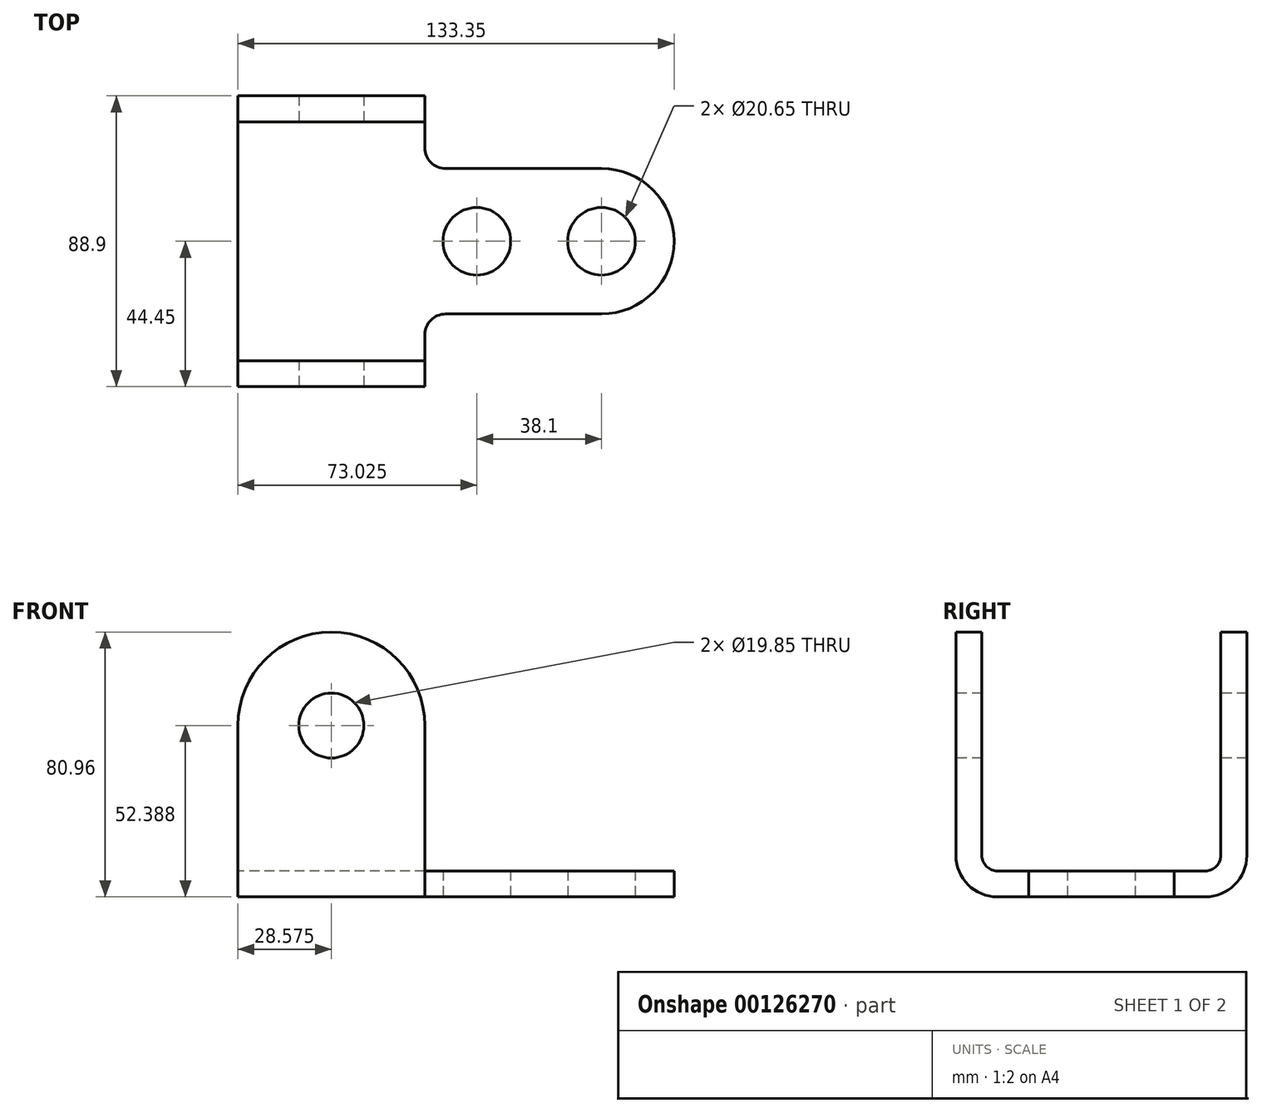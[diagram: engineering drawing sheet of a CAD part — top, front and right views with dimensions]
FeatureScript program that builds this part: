
annotation { "Feature Type Name" : "Feature", "Feature Type Description" : "" }
export const myFeature = defineFeature(function(context is Context, id is Id, definition is map)
    precondition{}
    {
        {
            var Q0;
            Q0=qCreatedBy(makeId("Top.planeOp"),FACE);
            var sketch = newSketch(context, id + "F0", { "sketchPlane" : qUnion([Q0])});
            skLineSegment(sketch, "E0", {"start": v(0, -44.45) * mm, "end": v(0, 44.45) * mm});
            skLineSegment(sketch, "E1", {"start": v(0, 44.45) * mm, "end": v(57.15, 44.45) * mm});
            skLineSegment(sketch, "E2", {"start": v(57.15, 44.45) * mm, "end": v(57.15, 28.57) * mm});
            skLineSegment(sketch, "E3", {"start": v(57.15, -44.45) * mm, "end": v(0, -44.45) * mm});
            skArc(sketch, "E4", {"start": v(111.12, 22.23) * mm, "mid": v(133.35, 0) * mm, "end": v(111.12, -22.23) * mm});
            skLineSegment(sketch, "E5", {"start": v(63.5, 22.22) * mm, "end": v(111.12, 22.23) * mm});
            skLineSegment(sketch, "E6", {"start": v(57.15, -44.45) * mm, "end": v(57.15, -28.58) * mm});
            skLineSegment(sketch, "E7", {"start": v(63.5, -22.23) * mm, "end": v(111.12, -22.23) * mm});
            skPoint(sketch, "E8.visualSharp", {"position": v(57.15, -22.23) * mm});
            skArc(sketch, "E8.filletArc", {"start": v(63.5, -22.23) * mm, "mid": v(59, -24.08) * mm, "end": v(57.15, -28.58) * mm});
            skPoint(sketch, "E9.visualSharp", {"position": v(57.15, 22.22) * mm});
            skArc(sketch, "E9.filletArc", {"start": v(57.15, 28.57) * mm, "mid": v(59, 24.08) * mm, "end": v(63.5, 22.22) * mm});
            skCircle(sketch, "E10", {"center": v(73.03, 0) * mm, "radius": 10.33 * mm});
            skCircle(sketch, "E11", {"center": v(111.12, 0) * mm, "radius": 10.33 * mm});
            skSolve(sketch);
        }
        {
            var Q0;
            Q0 = qSketchRegion(id + "F0", true);
            extrude(context, id + "F1", {"entities" : qUnion([Q0]), "depth" : 7.94 * mm});
        }
        {
            var Q0;
            Q0=makeQuery(id+"F1.opExtrude","SWEPT_FACE",FACE,{"disambiguationData":[OSD([sQuery(id+"F0.wireOp",EDGE,"E3")])]});
            var sketch = newSketch(context, id + "F2", { "sketchPlane" : qUnion([Q0])});
            skLineSegment(sketch, "E12", {"start": v(0, 7.94) * mm, "end": v(57.15, 7.94) * mm});
            skLineSegment(sketch, "E13", {"start": v(57.15, 7.94) * mm, "end": v(57.15, 52.39) * mm});
            skLineSegment(sketch, "E14", {"start": v(0, 7.94) * mm, "end": v(0, 52.39) * mm});
            skArc(sketch, "E15", {"start": v(0, 52.39) * mm, "mid": v(28.58, 80.96) * mm, "end": v(57.15, 52.39) * mm});
            skCircle(sketch, "E16", {"center": v(28.58, 52.39) * mm, "radius": 9.92 * mm});
            skSolve(sketch);
        }
        {
            var Q0;
            Q0 = qSketchRegion(id + "F2", true);
            extrude(context, id + "F3", {"entities" : qUnion([Q0]), "operationType" : NewBodyOperationType.ADD, "oppositeDirection" : true, "depth" : 88.9 * mm});
        }
        {
            var Q0;
            Q0=makeQuery(id+"F3.boolean.opBoolean","MERGE",FACE,{"derivedFrom":[makeQuery(id+"F1.opExtrude","SWEPT_FACE",FACE,{"disambiguationData":[OSD([sQuery(id+"F0.wireOp",EDGE,"E0")])]}),makeQuery(id+"F3.opExtrude","SWEPT_FACE",FACE,{"disambiguationData":[OSD([sQuery(id+"F2.wireOp",EDGE,"E14")])]})]});
            var sketch = newSketch(context, id + "F4", { "sketchPlane" : qUnion([Q0])});
            skLineSegment(sketch, "E17.bottom", {"start": v(-31.75, 7.94) * mm, "end": v(31.75, 7.94) * mm});
            skLineSegment(sketch, "E17.top", {"start": v(-36.51, 84.14) * mm, "end": v(36.51, 84.14) * mm});
            skLineSegment(sketch, "E17.left", {"start": v(-36.51, 12.7) * mm, "end": v(-36.51, 84.14) * mm});
            skLineSegment(sketch, "E17.right", {"start": v(36.51, 12.7) * mm, "end": v(36.51, 84.14) * mm});
            skPoint(sketch, "E18.visualSharp", {"position": v(-36.51, 7.94) * mm});
            skArc(sketch, "E18.filletArc", {"start": v(-36.51, 12.7) * mm, "mid": v(-35.12, 9.33) * mm, "end": v(-31.75, 7.94) * mm});
            skPoint(sketch, "E19.visualSharp", {"position": v(36.51, 7.94) * mm});
            skArc(sketch, "E19.filletArc", {"start": v(31.75, 7.94) * mm, "mid": v(35.12, 9.33) * mm, "end": v(36.51, 12.7) * mm});
            skSolve(sketch);
        }
        {
            var Q0;
            Q0 = qSketchRegion(id + "F4", true);
            extrude(context, id + "F5", {"entities" : qUnion([Q0]), "operationType" : NewBodyOperationType.REMOVE, "oppositeDirection" : true, "depth" : 57.15 * mm});
        }
        {
            var Q0;
            Q0=makeQuery(id+"F1.opExtrude","CAP_EDGE",EDGE,{"disambiguationData":[OSD([sQuery(id+"F0.wireOp",EDGE,"E1")])],"isStart":true});
            fillet(context, id + "F6", {"entities" : qUnion([Q0]), "radius" : 12.7 * mm, "tangentPropagation" : true, "allowEdgeOverflow" : false});
        }
        {
            var Q0;
            Q0=makeQuery(id+"F1.opExtrude","CAP_EDGE",EDGE,{"disambiguationData":[OSD([sQuery(id+"F0.wireOp",EDGE,"E3")])],"isStart":true});
            fillet(context, id + "F7", {"entities" : qUnion([Q0]), "radius" : 12.7 * mm, "tangentPropagation" : true, "allowEdgeOverflow" : false});
        }
    });
